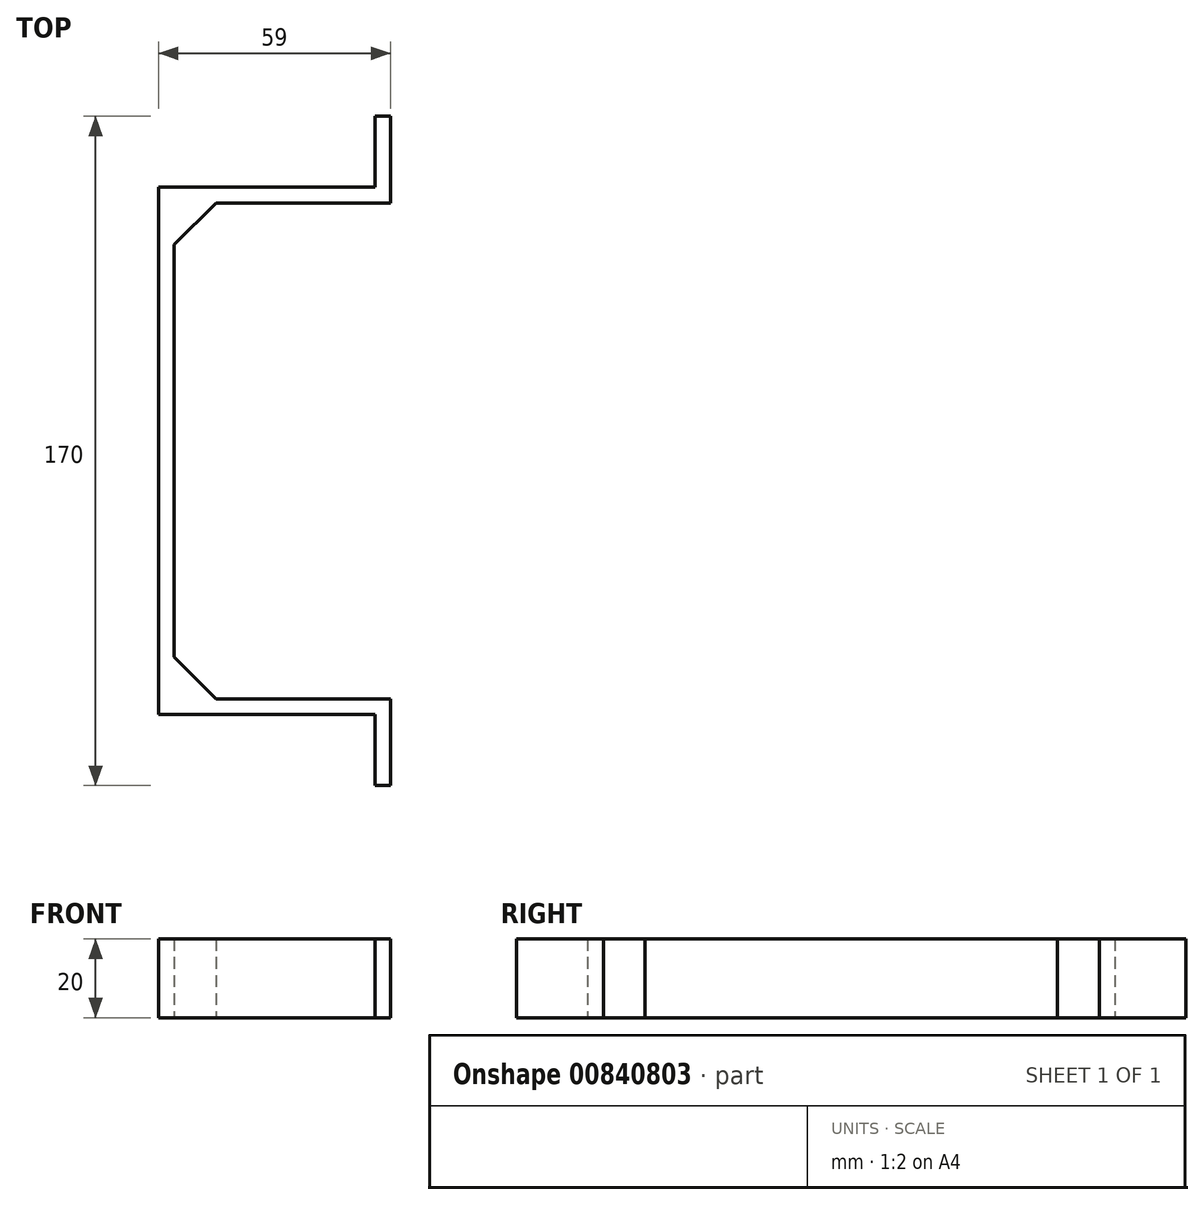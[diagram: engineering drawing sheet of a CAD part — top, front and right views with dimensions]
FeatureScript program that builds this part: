
annotation { "Feature Type Name" : "Feature", "Feature Type Description" : "" }
export const myFeature = defineFeature(function(context is Context, id is Id, definition is map)
    precondition{}
    {
        {
            var Q0;
            Q0=qCreatedBy(makeId("Top.planeOp"),FACE);
            var sketch = newSketch(context, id + "F0", { "sketchPlane" : qUnion([Q0])});
            skLineSegment(sketch, "E0", {"start": v(0, 0) * mm, "end": v(0, 65) * mm, "construction": true});
            skLineSegment(sketch, "E1", {"start": v(0, 65) * mm, "end": v(55, 65) * mm, "construction": true});
            skLineSegment(sketch, "E2", {"start": v(55, 65) * mm, "end": v(55, 85) * mm, "construction": true});
            skLineSegment(sketch, "E3", {"start": v(0, 0) * mm, "end": v(-32.92, 0) * mm, "construction": true});
            skLineSegment(sketch, "E4.MirrorCS", {"start": v(0, -65) * mm, "end": v(55, -65) * mm, "construction": true});
            skLineSegment(sketch, "E5.MirrorCS", {"start": v(0, 0) * mm, "end": v(0, -65) * mm, "construction": true});
            skLineSegment(sketch, "E6.MirrorCS", {"start": v(55, -65) * mm, "end": v(55, -85) * mm, "construction": true});
            skLineSegment(sketch, "E7.0", {"start": v(53, 67) * mm, "end": v(53, 85) * mm});
            skLineSegment(sketch, "E7.1", {"start": v(-2, 67) * mm, "end": v(53, 67) * mm});
            skLineSegment(sketch, "E7.2", {"start": v(53, -67) * mm, "end": v(53, -85) * mm});
            skLineSegment(sketch, "E7.3", {"start": v(-2, -67) * mm, "end": v(53, -67) * mm});
            skLineSegment(sketch, "E7.4", {"start": v(-2, 0) * mm, "end": v(-2, -67) * mm});
            skLineSegment(sketch, "E7.5", {"start": v(-2, 0) * mm, "end": v(-2, 67) * mm});
            skLineSegment(sketch, "E8.0", {"start": v(57, 63) * mm, "end": v(57, 85) * mm});
            skLineSegment(sketch, "E8.1", {"start": v(12.6, 63) * mm, "end": v(57, 63) * mm});
            skLineSegment(sketch, "E8.2", {"start": v(57, -63) * mm, "end": v(57, -85) * mm});
            skLineSegment(sketch, "E8.3", {"start": v(12.6, -63) * mm, "end": v(57, -63) * mm});
            skLineSegment(sketch, "E8.4", {"start": v(2, -0.5) * mm, "end": v(2, -52.4) * mm});
            skLineSegment(sketch, "E8.5", {"start": v(2, -0.5) * mm, "end": v(2, 52.4) * mm});
            skLineSegment(sketch, "E9", {"start": v(53, -85) * mm, "end": v(57, -85) * mm});
            skLineSegment(sketch, "E10", {"start": v(57, 85) * mm, "end": v(53, 85) * mm});
            skLineSegment(sketch, "E11", {"start": v(2, 52.4) * mm, "end": v(12.6, 63) * mm});
            skLineSegment(sketch, "E12.MirrorCS", {"start": v(2, -52.4) * mm, "end": v(12.6, -63) * mm});
            skSolve(sketch);
        }
        {
            var Q0;
            Q0 = qSketchRegion(id + "F0", true);
            extrude(context, id + "F1", {"entities" : qUnion([Q0]), "depth" : 20 * mm, "offsetDistance" : 25 * mm});
        }
    });
